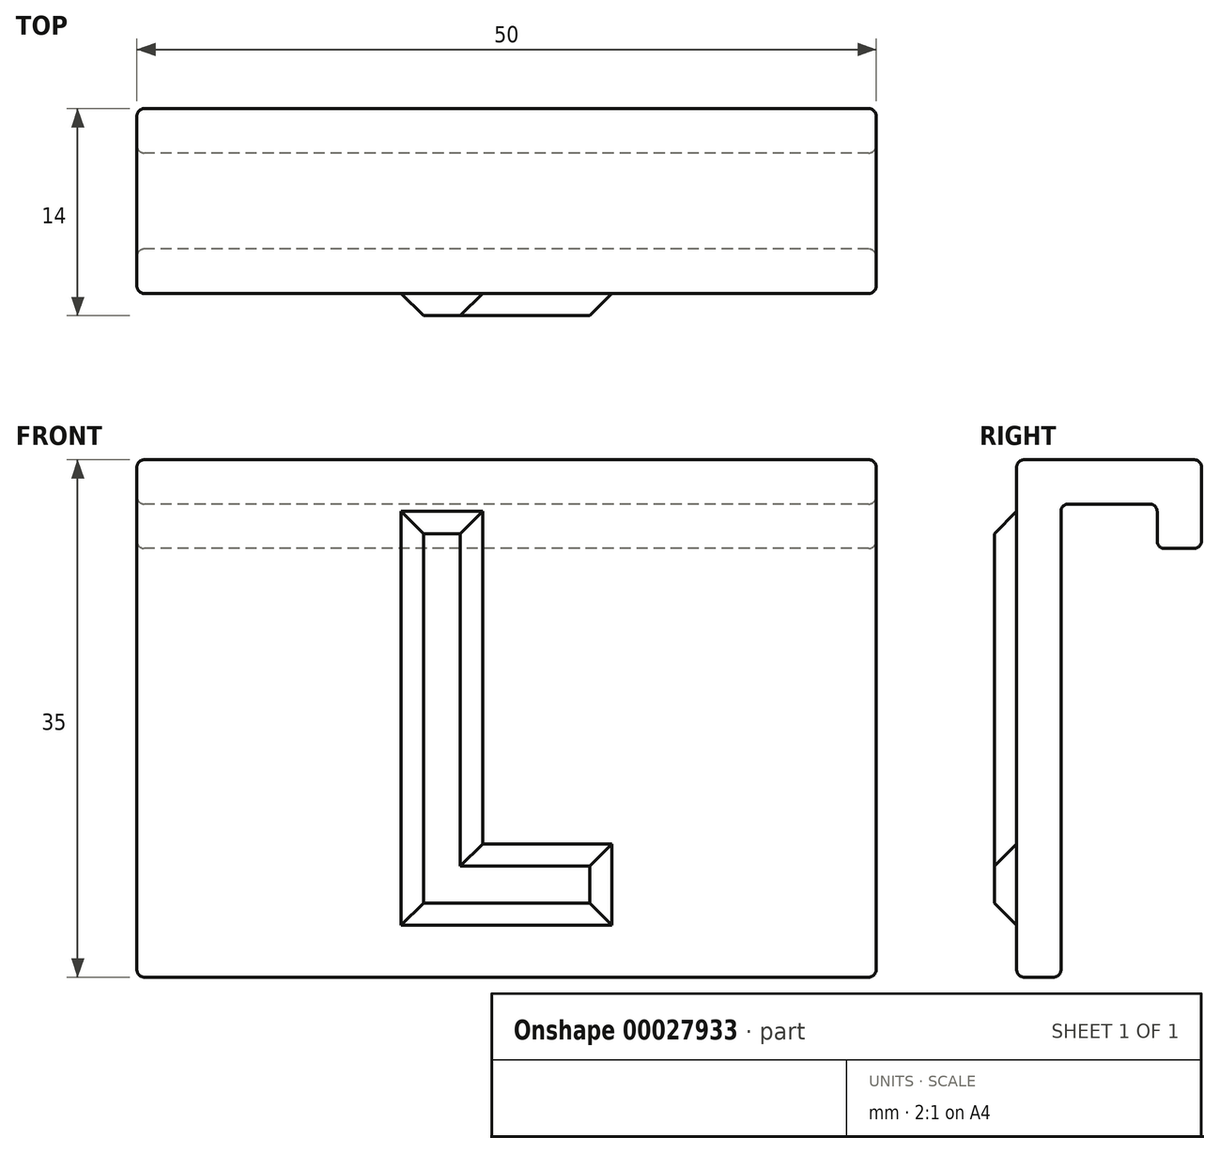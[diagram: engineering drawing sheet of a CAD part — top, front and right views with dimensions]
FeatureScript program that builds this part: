
annotation { "Feature Type Name" : "Feature", "Feature Type Description" : "" }
export const myFeature = defineFeature(function(context is Context, id is Id, definition is map)
    precondition{}
    {
        {
            var Q0;
            Q0=qCreatedBy(makeId("Right.planeOp"),FACE);
            var sketch = newSketch(context, id + "F0", { "sketchPlane" : qUnion([Q0])});
            skLineSegment(sketch, "E0", {"start": v(0, 0) * mm, "end": v(0, 35) * mm});
            skLineSegment(sketch, "E1", {"start": v(0, 35) * mm, "end": v(12.5, 35) * mm});
            skLineSegment(sketch, "E2", {"start": v(12.5, 35) * mm, "end": v(12.5, 29) * mm});
            skLineSegment(sketch, "E3", {"start": v(12.5, 29) * mm, "end": v(9.5, 29) * mm});
            skLineSegment(sketch, "E4", {"start": v(9.5, 29) * mm, "end": v(9.5, 32) * mm});
            skLineSegment(sketch, "E5", {"start": v(9.5, 32) * mm, "end": v(3, 32) * mm});
            skLineSegment(sketch, "E6", {"start": v(3, 32) * mm, "end": v(3, 0) * mm});
            skLineSegment(sketch, "E7", {"start": v(3, 0) * mm, "end": v(0, 0) * mm});
            skSolve(sketch);
        }
        {
            var Q0;
            Q0=qSketchRegion(id+"F0",true);
            extrude(context, id + "F1", {"entities" : qUnion([Q0]), "depth" : 50 * mm});
        }
        {
            var Q0;
            Q0=makeQuery(id+"F1.opExtrude","SWEPT_FACE",FACE,{"disambiguationData":[OSD([sQuery(id+"F0.wireOp",EDGE,"E0")])]});
            var sketch = newSketch(context, id + "F2", { "sketchPlane" : qUnion([Q0])});
            skLineSegment(sketch, "E8", {"start": v(17.5, 35) * mm, "end": v(17.5, 0) * mm});
            skLineSegment(sketch, "E9", {"start": v(32.5, 35) * mm, "end": v(32.5, 0) * mm});
            skLineSegment(sketch, "E10", {"start": v(0, 5) * mm, "end": v(50, 5) * mm});
            skLineSegment(sketch, "E11", {"start": v(2.5, 35) * mm, "end": v(2.5, 0) * mm});
            skLineSegment(sketch, "E12", {"start": v(47.5, 35) * mm, "end": v(47.5, 0) * mm});
            skLineSegment(sketch, "E13", {"start": v(5, 30) * mm, "end": v(6.86, 30) * mm});
            skLineSegment(sketch, "E14", {"start": v(7.5, 5) * mm, "end": v(5, 5) * mm});
            skPoint(sketch, "E15", {"position": v(2.5, 30) * mm});
            skPoint(sketch, "E16", {"position": v(17.5, 30) * mm});
            skPoint(sketch, "E17", {"position": v(32.5, 30) * mm});
            skPoint(sketch, "E18", {"position": v(47.5, 30) * mm});
            skPoint(sketch, "E19", {"position": v(47.5, 5) * mm});
            skPoint(sketch, "E20", {"position": v(32.5, 5) * mm});
            skPoint(sketch, "E21", {"position": v(17.5, 5) * mm});
            skPoint(sketch, "E22", {"position": v(2.5, 5) * mm});
            skLineSegment(sketch, "E23", {"start": v(2.5, 30) * mm, "end": v(5, 30) * mm});
            skLineSegment(sketch, "E24", {"start": v(5, 30) * mm, "end": v(5, 5) * mm});
            skLineSegment(sketch, "E25", {"start": v(17.5, 30) * mm, "end": v(16.25, 30) * mm});
            skLineSegment(sketch, "E26", {"start": v(16.25, 30) * mm, "end": v(16.25, 27.5) * mm});
            skPoint(sketch, "E27", {"position": v(5, 17.5) * mm});
            skLineSegment(sketch, "E28", {"start": v(5, 17.5) * mm, "end": v(5, 20) * mm});
            skLineSegment(sketch, "E29", {"start": v(16.25, 27.5) * mm, "end": v(16.25, 20) * mm});
            skLineSegment(sketch, "E30", {"start": v(7.5, 5) * mm, "end": v(7.5, 17.5) * mm});
            skLineSegment(sketch, "E31", {"start": v(7.5, 20) * mm, "end": v(7.5, 27.5) * mm});
            skLineSegment(sketch, "E32", {"start": v(16.25, 30) * mm, "end": v(13.75, 30) * mm});
            skLineSegment(sketch, "E33", {"start": v(5, 30) * mm, "end": v(13.75, 30) * mm});
            skLineSegment(sketch, "E34", {"start": v(13.75, 30) * mm, "end": v(16.25, 27.5) * mm});
            skLineSegment(sketch, "E35", {"start": v(13.75, 26.46) * mm, "end": v(13.75, 21.04) * mm});
            skLineSegment(sketch, "E36", {"start": v(7.5, 17.5) * mm, "end": v(13.75, 17.5) * mm});
            skLineSegment(sketch, "E37", {"start": v(13.75, 17.5) * mm, "end": v(16.25, 20) * mm});
            skPoint(sketch, "E38.trimOffspring.end.orphan", {"position": v(0, 30) * mm});
            skPoint(sketch, "E39.orphan", {"position": v(13.75, 20) * mm});
            skPoint(sketch, "E40.orphan", {"position": v(15, 18.75) * mm});
            skPoint(sketch, "E41.orphan", {"position": v(13.75, 27.5) * mm});
            skPoint(sketch, "E42.start.orphan", {"position": v(15, 28.75) * mm});
            skLineSegment(sketch, "E43", {"start": v(17.5, 30) * mm, "end": v(19.38, 30) * mm});
            skLineSegment(sketch, "E44", {"start": v(19.38, 30) * mm, "end": v(19.38, 5) * mm});
            skLineSegment(sketch, "E45", {"start": v(19.38, 5) * mm, "end": v(30.62, 5) * mm});
            skLineSegment(sketch, "E46", {"start": v(30.62, 5) * mm, "end": v(32.5, 5) * mm});
            skLineSegment(sketch, "E47", {"start": v(30.62, 5) * mm, "end": v(30.62, 7.5) * mm});
            skLineSegment(sketch, "E48", {"start": v(30.62, 7.5) * mm, "end": v(21.88, 7.5) * mm});
            skLineSegment(sketch, "E49", {"start": v(21.88, 7.5) * mm, "end": v(21.88, 30) * mm});
            skLineSegment(sketch, "E50", {"start": v(21.88, 30) * mm, "end": v(19.38, 30) * mm});
            skLineSegment(sketch, "E51", {"start": v(32.5, 5) * mm, "end": v(33.75, 5) * mm});
            skLineSegment(sketch, "E52", {"start": v(33.75, 5) * mm, "end": v(36.25, 5) * mm});
            skLineSegment(sketch, "E53", {"start": v(47.5, 5) * mm, "end": v(45, 5) * mm});
            skLineSegment(sketch, "E54", {"start": v(45, 5) * mm, "end": v(42.5, 5) * mm});
            skLineSegment(sketch, "E55", {"start": v(36.25, 5) * mm, "end": v(42.5, 5) * mm});
            skLineSegment(sketch, "E56", {"start": v(39.37, 30) * mm, "end": v(37.5, 30) * mm});
            skLineSegment(sketch, "E57", {"start": v(39.37, 30) * mm, "end": v(41.25, 30) * mm});
            skLineSegment(sketch, "E58", {"start": v(37.5, 30) * mm, "end": v(33.75, 5) * mm});
            skLineSegment(sketch, "E59", {"start": v(41.25, 30) * mm, "end": v(45, 5) * mm});
            skLineSegment(sketch, "E60", {"start": v(36.25, 5) * mm, "end": v(37.75, 15) * mm});
            skLineSegment(sketch, "E61", {"start": v(42.5, 5) * mm, "end": v(41, 15) * mm});
            skLineSegment(sketch, "E62", {"start": v(38.12, 17.5) * mm, "end": v(40.62, 17.5) * mm});
            skLineSegment(sketch, "E63.trimOffspring", {"start": v(38.12, 17.5) * mm, "end": v(39.37, 25.83) * mm});
            skLineSegment(sketch, "E64.trimOffspring", {"start": v(40.62, 17.5) * mm, "end": v(39.38, 25.83) * mm});
            skPoint(sketch, "E65.orphan", {"position": v(39.38, 5) * mm});
            skLineSegment(sketch, "E66", {"start": v(39.6, 15) * mm, "end": v(37.75, 15) * mm});
            skLineSegment(sketch, "E67", {"start": v(39.6, 15) * mm, "end": v(41, 15) * mm});
            skPoint(sketch, "E68.orphan", {"position": v(37.81, 15.42) * mm});
            skPoint(sketch, "E69.orphan", {"position": v(40.94, 15.42) * mm});
            skPoint(sketch, "E70.start.orphan", {"position": v(39.37, 17.5) * mm});
            skLineSegment(sketch, "E71", {"start": v(13.23, 26.98) * mm, "end": v(13.75, 26.46) * mm});
            skLineSegment(sketch, "E72", {"start": v(13.23, 26.98) * mm, "end": v(12.71, 27.5) * mm});
            skLineSegment(sketch, "E73", {"start": v(12.71, 27.5) * mm, "end": v(7.5, 27.5) * mm});
            skLineSegment(sketch, "E74", {"start": v(13.75, 21.04) * mm, "end": v(12.71, 20) * mm});
            skLineSegment(sketch, "E75", {"start": v(7.5, 20) * mm, "end": v(12.71, 20) * mm});
            skSolve(sketch);
        }
        {
            var Q0;
            {var subQ6=sQuery(id+"F2.wireOp",EDGE,"E14");Q0=makeQuery(id+"F2.imprint","IMPRINT",FACE,{"disambiguationData":[TD([[makeQuery(id+"F2.imprint","IMPRINT",EDGE,{"derivedFrom":subQ6}),-1.0]])]});}
            var Q1;
            Q1=makeQuery(id+"F2.imprint","IMPRINT",FACE,{"disambiguationData":[TD([[makeQuery(id+"F2.imprint","IMPRINT",EDGE,{"derivedFrom":sQuery(id+"F2.wireOp",EDGE,"E44")}),1.0]])]});
            var Q2;
            Q2=makeQuery(id+"F2.imprint","IMPRINT",FACE,{"disambiguationData":[TD([[makeQuery(id+"F2.imprint","IMPRINT",EDGE,{"derivedFrom":sQuery(id+"F2.wireOp",EDGE,"E52")}),1.0]])]});
            extrude(context, id + "F3", {"entities" : qUnion([Q0, Q1, Q2]), "operationType" : NewBodyOperationType.ADD, "depth" : 1.5 * mm});
        }
        {
            var Q0;
            Q0=makeQuery(id+"F1.opExtrude","SWEPT_FACE",FACE,{"disambiguationData":[OSD([sQuery(id+"F0.wireOp",EDGE,"E1")])]});
            var Q1;
            Q1=makeQuery(id+"F1.opExtrude","CAP_FACE",FACE,{"disambiguationData":[OSD([sQuery(id+"F0.wireOp",EDGE,"E0"),sQuery(id+"F0.wireOp",EDGE,"E1"),sQuery(id+"F0.wireOp",EDGE,"E2"),sQuery(id+"F0.wireOp",EDGE,"E3"),sQuery(id+"F0.wireOp",EDGE,"E4"),sQuery(id+"F0.wireOp",EDGE,"E5"),sQuery(id+"F0.wireOp",EDGE,"E6"),sQuery(id+"F0.wireOp",EDGE,"E7")])],"isStart":false});
            var Q2;
            Q2=makeQuery(id+"F1.opExtrude","CAP_FACE",FACE,{"disambiguationData":[OSD([sQuery(id+"F0.wireOp",EDGE,"E0"),sQuery(id+"F0.wireOp",EDGE,"E1"),sQuery(id+"F0.wireOp",EDGE,"E2"),sQuery(id+"F0.wireOp",EDGE,"E3"),sQuery(id+"F0.wireOp",EDGE,"E4"),sQuery(id+"F0.wireOp",EDGE,"E5"),sQuery(id+"F0.wireOp",EDGE,"E6"),sQuery(id+"F0.wireOp",EDGE,"E7")])],"isStart":true});
            var Q3;
            Q3=makeQuery(id+"F1.opExtrude","SWEPT_FACE",FACE,{"disambiguationData":[OSD([sQuery(id+"F0.wireOp",EDGE,"E2")])]});
            var Q4;
            Q4=makeQuery(id+"F1.opExtrude","SWEPT_FACE",FACE,{"disambiguationData":[OSD([sQuery(id+"F0.wireOp",EDGE,"E3")])]});
            var Q5;
            Q5=makeQuery(id+"F1.opExtrude","SWEPT_FACE",FACE,{"disambiguationData":[OSD([sQuery(id+"F0.wireOp",EDGE,"E5")])]});
            var Q6;
            Q6=makeQuery(id+"F1.opExtrude","SWEPT_FACE",FACE,{"disambiguationData":[OSD([sQuery(id+"F0.wireOp",EDGE,"E6")])]});
            var Q7;
            Q7=makeQuery(id+"F1.opExtrude","SWEPT_FACE",FACE,{"disambiguationData":[OSD([sQuery(id+"F0.wireOp",EDGE,"E7")])]});
            fillet(context, id + "F4", {"entities" : qUnion([Q0, Q1, Q2, Q3, Q4, Q5, Q6, Q7]), "radius" : .5 * mm, "tangentPropagation" : true, "allowEdgeOverflow" : false});
        }
        {
            var Q0;
            {var subQ0=sQuery(id+"F0.wireOp",EDGE,"E0");var subQ1=sQuery(id+"F0.wireOp",EDGE,"E1");Q0=makeQuery(id+"F3.boolean.opBoolean","SPLIT",FACE,{"disambiguationData":[TD([makeQuery(id+"F1.opExtrude","SWEPT_FACE",FACE,{"disambiguationData":[OSD([subQ1])]})])],"derivedFrom":makeQuery(id+"F1.opExtrude","SWEPT_FACE",FACE,{"disambiguationData":[OSD([subQ0])]})});}
            var Q1;
            Q1=makeQuery(id+"F3.boolean.opBoolean","SPLIT",FACE,{"disambiguationData":[TD([makeQuery(id+"F3.opExtrude","SWEPT_FACE",FACE,{"disambiguationData":[OSD([sQuery(id+"F2.wireOp",EDGE,"E31")])]})])],"derivedFrom":makeQuery(id+"F1.opExtrude","SWEPT_FACE",FACE,{"disambiguationData":[OSD([sQuery(id+"F0.wireOp",EDGE,"E0")])]})});
            var Q2;
            Q2=makeQuery(id+"F3.opExtrude","CAP_EDGE",EDGE,{"disambiguationData":[OSD([sQuery(id+"F2.wireOp",EDGE,"E62")])],"isStart":true});
            chamfer(context, id + "F5", {"entities" : qUnion([Q0, Q1, Q2]), "width" : 1.5 * mm, "tangentPropagation" : true});
        }
    });
